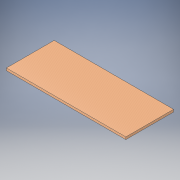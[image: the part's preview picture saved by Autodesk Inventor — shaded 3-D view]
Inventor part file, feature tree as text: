
AUTODESK INVENTOR PART (.ipt)
format: ipt  version: 2019 (Build 230136000, 136)  size: 105,472 bytes
history: native  units: mm
features: extrude x1, sketch x1
ambient origin geometry x8: Origin, YZ Plane, XZ Plane, XY Plane, X Axis, Y Axis, Z Axis, Center Point
bodies: Solid1 (feature_tree)
feature tree (2):
  extrude  "Extrusion1"  Depth=10000.0mm
  sketch  "Sketch1"  dims[d0=25000.0mm d1=10000.0mm d2=500.0mm d3=0.0mm]
